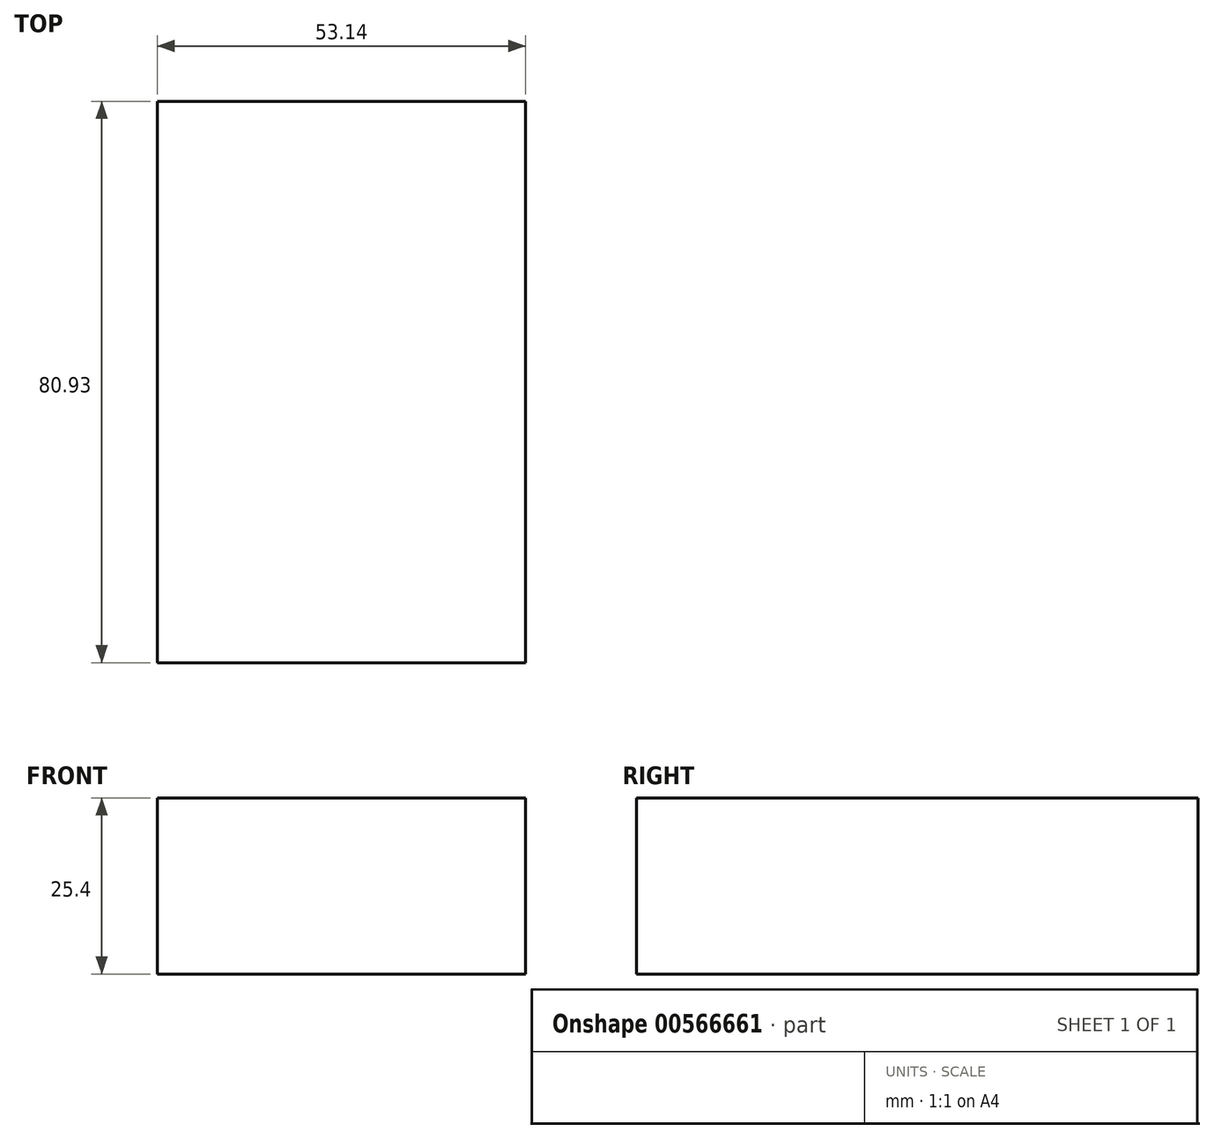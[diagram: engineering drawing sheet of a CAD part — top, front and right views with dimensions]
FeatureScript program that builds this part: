
annotation { "Feature Type Name" : "Feature", "Feature Type Description" : "" }
export const myFeature = defineFeature(function(context is Context, id is Id, definition is map)
    precondition{}
    {
        {
            var Q0;
            Q0=qCreatedBy(makeId("Top.planeOp"),FACE);
            var sketch = newSketch(context, id + "F0", { "sketchPlane" : qUnion([Q0])});
            skLineSegment(sketch, "E0.bottom", {"start": v(-38.48, 29.93) * mm, "end": v(14.66, 29.93) * mm});
            skLineSegment(sketch, "E0.top", {"start": v(-38.48, -51) * mm, "end": v(14.66, -51) * mm});
            skLineSegment(sketch, "E0.left", {"start": v(-38.48, 29.93) * mm, "end": v(-38.48, -51) * mm});
            skLineSegment(sketch, "E0.right", {"start": v(14.66, 29.93) * mm, "end": v(14.66, -51) * mm});
            skSolve(sketch);
        }
        {
            var Q0;
            Q0=makeQuery(id+"F0.imprint","IMPRINT",FACE,{"disambiguationData":[TD([[makeQuery(id+"F0.imprint","IMPRINT",EDGE,{"derivedFrom":sQuery(id+"F0.wireOp",EDGE,"E0.bottom")}),-1.0]])]});
            extrude(context, id + "F1", {"entities" : qUnion([Q0]), "oppositeDirection" : true, "depth" : 25.4 * mm, "offsetDistance" : 25.4 * mm});
        }
    });
